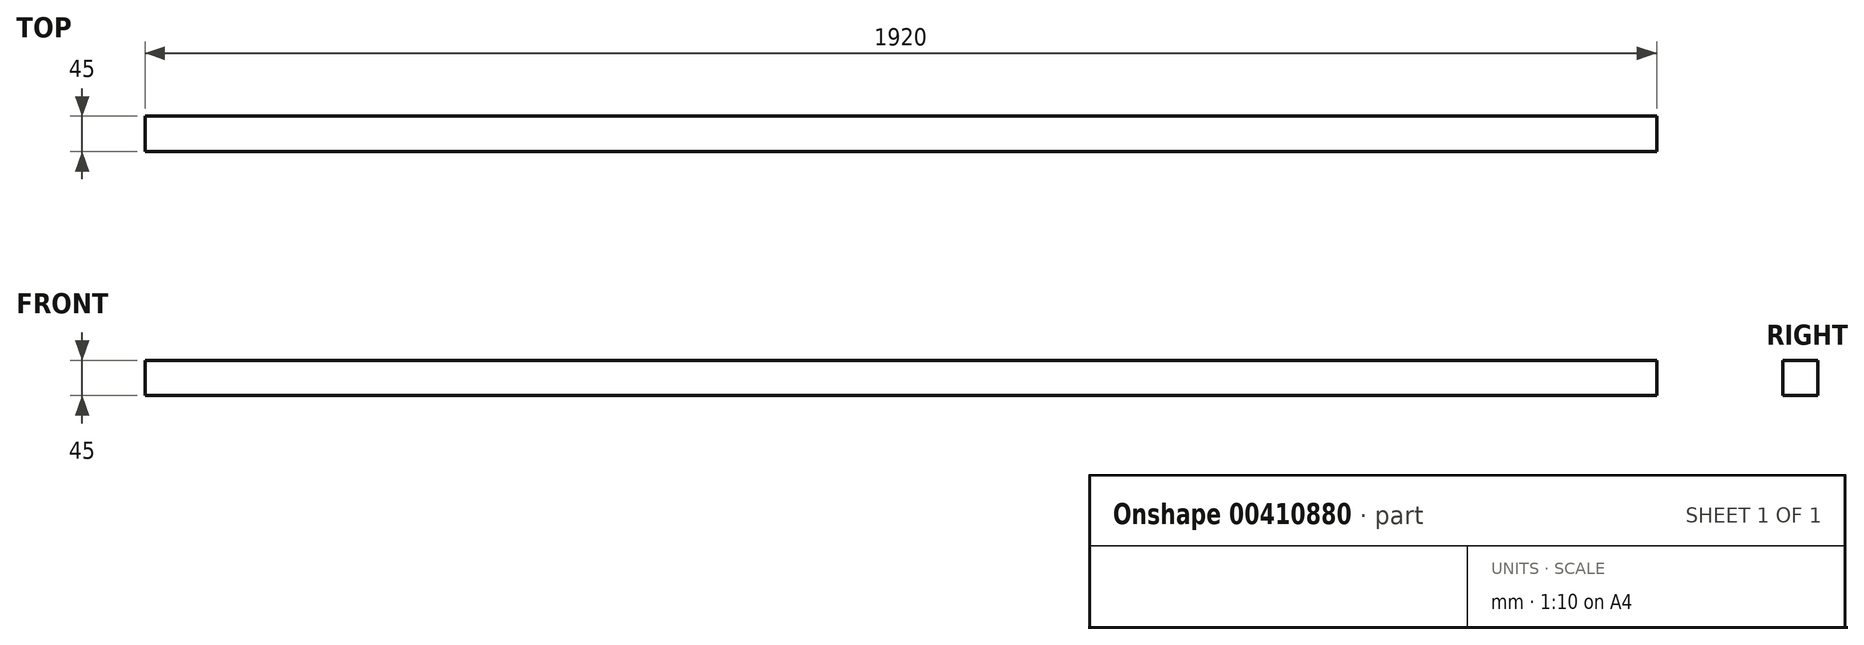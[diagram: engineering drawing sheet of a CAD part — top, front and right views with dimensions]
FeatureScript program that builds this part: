
annotation { "Feature Type Name" : "Feature", "Feature Type Description" : "" }
export const myFeature = defineFeature(function(context is Context, id is Id, definition is map)
    precondition{}
    {
        {
            var Q0;
            Q0=qCreatedBy(makeId("Top.planeOp"),FACE);
            var sketch = newSketch(context, id + "F0", { "sketchPlane" : qUnion([Q0])});
            skLineSegment(sketch, "E0.bottom", {"start": v(-955.77, -68.6) * mm, "end": v(964.23, -68.6) * mm});
            skLineSegment(sketch, "E0.top", {"start": v(-955.77, -113.6) * mm, "end": v(964.23, -113.6) * mm});
            skLineSegment(sketch, "E0.left", {"start": v(-955.77, -68.6) * mm, "end": v(-955.77, -113.6) * mm});
            skLineSegment(sketch, "E0.right", {"start": v(964.23, -68.6) * mm, "end": v(964.23, -113.6) * mm});
            skSolve(sketch);
        }
        {
            var Q0;
            Q0 = qSketchRegion(id + "F0", true);
            extrude(context, id + "F1", {"entities" : qUnion([Q0]), "depth" : 45 * mm});
        }
    });
